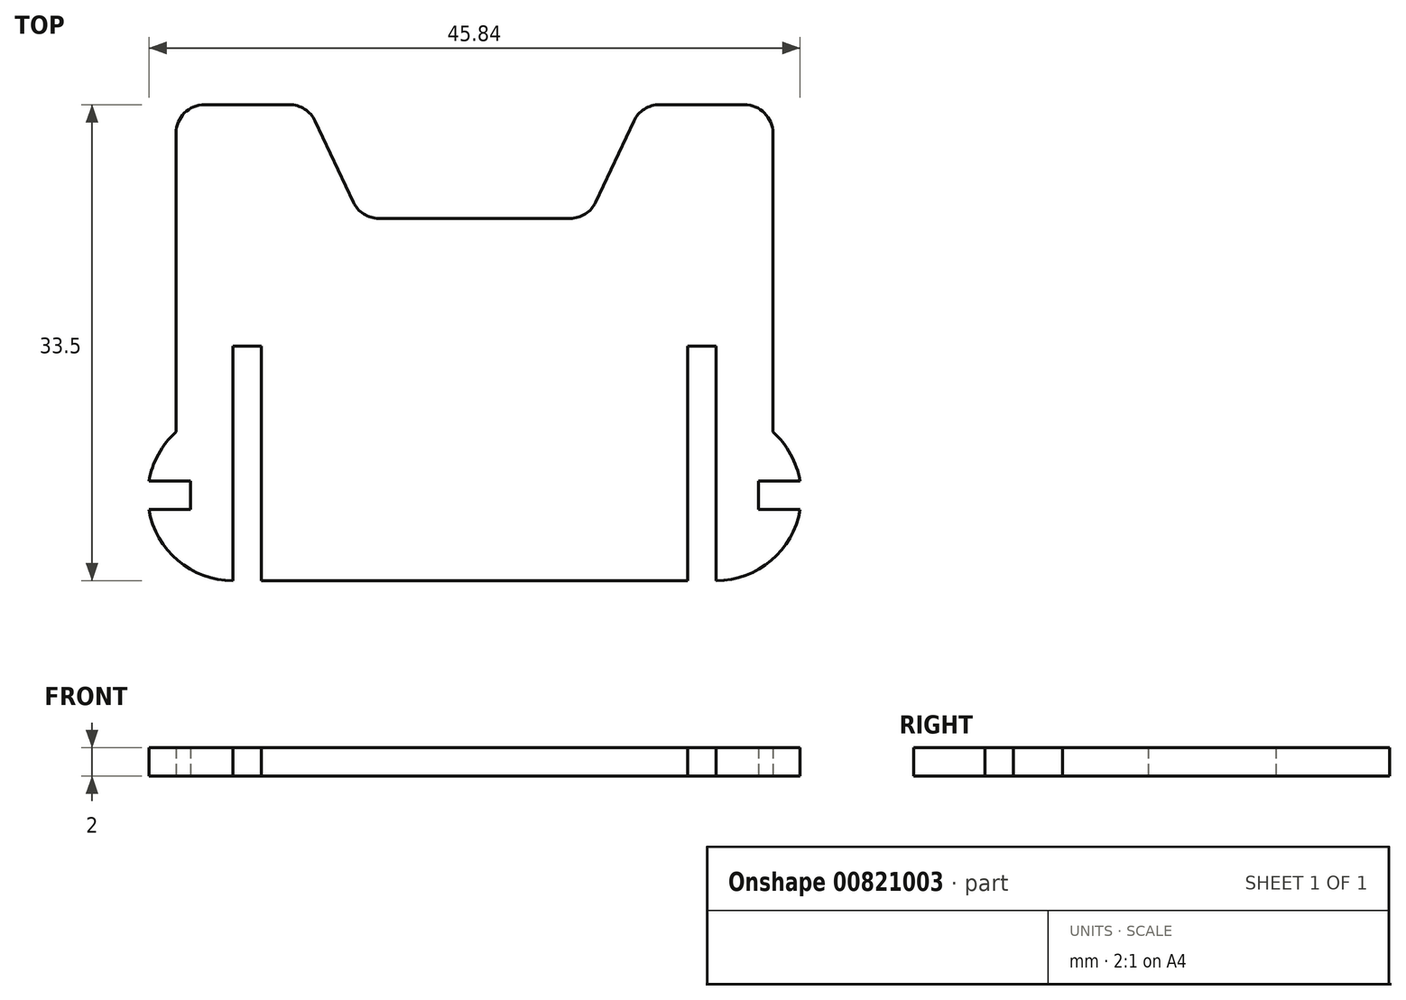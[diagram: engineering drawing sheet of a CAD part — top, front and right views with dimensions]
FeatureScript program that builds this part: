
annotation { "Feature Type Name" : "Feature", "Feature Type Description" : "" }
export const myFeature = defineFeature(function(context is Context, id is Id, definition is map)
    precondition{}
    {
        {
            var Q0;
            Q0=qCreatedBy(makeId("Top.planeOp"),FACE);
            var sketch = newSketch(context, id + "F0", { "sketchPlane" : qUnion([Q0])});
            skLineSegment(sketch, "E0.bottom", {"start": v(-19, 16.75) * mm, "end": v(-13.02, 16.75) * mm});
            skLineSegment(sketch, "E0.top", {"start": v(-15, -16.75) * mm, "end": v(15, -16.75) * mm});
            skLineSegment(sketch, "E0.left", {"start": v(-21, 14.75) * mm, "end": v(-21, -6.28) * mm});
            skLineSegment(sketch, "E0.right", {"start": v(21, 14.75) * mm, "end": v(21, -6.28) * mm});
            skPoint(sketch, "E0.middle", {"position": v(0, 0) * mm});
            skPoint(sketch, "E1.middle", {"position": v(0, 8.75) * mm});
            skLineSegment(sketch, "E2", {"start": v(-11.21, 15.6) * mm, "end": v(-8.54, 9.9) * mm});
            skLineSegment(sketch, "E3", {"start": v(8.54, 9.9) * mm, "end": v(11.21, 15.6) * mm});
            skLineSegment(sketch, "E4.trimOffspring", {"start": v(-6.73, 8.75) * mm, "end": v(6.73, 8.75) * mm});
            skPoint(sketch, "E5.start.orphan", {"position": v(-21, 8.75) * mm});
            skPoint(sketch, "E6.orphan", {"position": v(-11.75, 0.75) * mm});
            skPoint(sketch, "E7.orphan", {"position": v(21, 8.75) * mm});
            skPoint(sketch, "E8.top.end.orphan", {"position": v(11.75, 0.75) * mm});
            skPoint(sketch, "E1.top.end.orphan", {"position": v(8, 0.75) * mm});
            skPoint(sketch, "E1.top.start.orphan", {"position": v(-8, 0.75) * mm});
            skLineSegment(sketch, "E9.trimOffspring", {"start": v(13.02, 16.75) * mm, "end": v(19, 16.75) * mm});
            skPoint(sketch, "E10.orphan", {"position": v(-8, 16.75) * mm});
            skPoint(sketch, "E11.visualSharp", {"position": v(-8, 8.75) * mm});
            skArc(sketch, "E11.filletArc", {"start": v(-8.54, 9.9) * mm, "mid": v(-7.8, 9.06) * mm, "end": v(-6.73, 8.75) * mm});
            skPoint(sketch, "E12.visualSharp", {"position": v(8, 8.75) * mm});
            skArc(sketch, "E12.filletArc", {"start": v(6.73, 8.75) * mm, "mid": v(7.8, 9.06) * mm, "end": v(8.54, 9.9) * mm});
            skPoint(sketch, "E13.visualSharp", {"position": v(-11.75, 16.75) * mm});
            skArc(sketch, "E13.filletArc", {"start": v(-11.21, 15.6) * mm, "mid": v(-11.95, 16.44) * mm, "end": v(-13.02, 16.75) * mm});
            skPoint(sketch, "E14.visualSharp", {"position": v(11.75, 16.75) * mm});
            skArc(sketch, "E14.filletArc", {"start": v(13.02, 16.75) * mm, "mid": v(11.95, 16.44) * mm, "end": v(11.21, 15.6) * mm});
            skPoint(sketch, "E15.visualSharp", {"position": v(-21, 16.75) * mm});
            skArc(sketch, "E15.filletArc", {"start": v(-19, 16.75) * mm, "mid": v(-20.41, 16.16) * mm, "end": v(-21, 14.75) * mm});
            skPoint(sketch, "E16.visualSharp", {"position": v(21, 16.75) * mm});
            skArc(sketch, "E16.filletArc", {"start": v(21, 14.75) * mm, "mid": v(20.41, 16.16) * mm, "end": v(19, 16.75) * mm});
            skArc(sketch, "E17", {"start": v(-21, -6.28) * mm, "mid": v(-22.25, -7.85) * mm, "end": v(-22.92, -9.75) * mm});
            skPoint(sketch, "E18.orphan", {"position": v(-21, -16.75) * mm});
            skLineSegment(sketch, "E19", {"start": v(-17, -0.25) * mm, "end": v(-15, -0.25) * mm});
            skPoint(sketch, "E20.orphan", {"position": v(-15, -10.75) * mm});
            skLineSegment(sketch, "E21", {"start": v(-15, -0.25) * mm, "end": v(-15, -16.75) * mm});
            skLineSegment(sketch, "E22", {"start": v(-17, -0.25) * mm, "end": v(-17, -16.75) * mm});
            skPoint(sketch, "E23.start.orphan", {"position": v(-17, 10.68) * mm});
            skLineSegment(sketch, "E24.MirrorCS", {"start": v(17, -0.25) * mm, "end": v(15, -0.25) * mm});
            skLineSegment(sketch, "E25.MirrorCS", {"start": v(17, -0.25) * mm, "end": v(17, -16.75) * mm});
            skLineSegment(sketch, "E26.MirrorCS", {"start": v(15, -0.25) * mm, "end": v(15, -16.75) * mm});
            skArc(sketch, "E27.MirrorCS", {"start": v(21, -6.28) * mm, "mid": v(22.25, -7.85) * mm, "end": v(22.92, -9.75) * mm});
            skPoint(sketch, "E28.orphan", {"position": v(21, -16.75) * mm});
            skLineSegment(sketch, "E29", {"start": v(-20, -9.75) * mm, "end": v(-22.92, -9.75) * mm});
            skLineSegment(sketch, "E30", {"start": v(-20, -11.75) * mm, "end": v(-22.92, -11.75) * mm});
            skLineSegment(sketch, "E31", {"start": v(-20, -11.75) * mm, "end": v(-20, -9.75) * mm});
            skArc(sketch, "E32.trimOffspring", {"start": v(-22.92, -11.75) * mm, "mid": v(-20.87, -15.33) * mm, "end": v(-17, -16.75) * mm});
            skPoint(sketch, "E33.end.orphan", {"position": v(-23, -10.75) * mm});
            skLineSegment(sketch, "E34.MirrorCS", {"start": v(20, -11.75) * mm, "end": v(20, -9.75) * mm});
            skLineSegment(sketch, "E35.MirrorCS", {"start": v(20, -9.75) * mm, "end": v(22.92, -9.75) * mm});
            skLineSegment(sketch, "E36.MirrorCS", {"start": v(20, -11.75) * mm, "end": v(22.92, -11.75) * mm});
            skArc(sketch, "E37.trimOffspring", {"start": v(22.92, -11.75) * mm, "mid": v(20.87, -15.33) * mm, "end": v(17, -16.75) * mm});
            skSolve(sketch);
        }
        {
            var Q0;
            Q0 = qSketchRegion(id + "F0", true);
            extrude(context, id + "F1", {"entities" : qUnion([Q0]), "depth" : 2 * mm, "offsetDistance" : 25 * mm});
        }
    });
